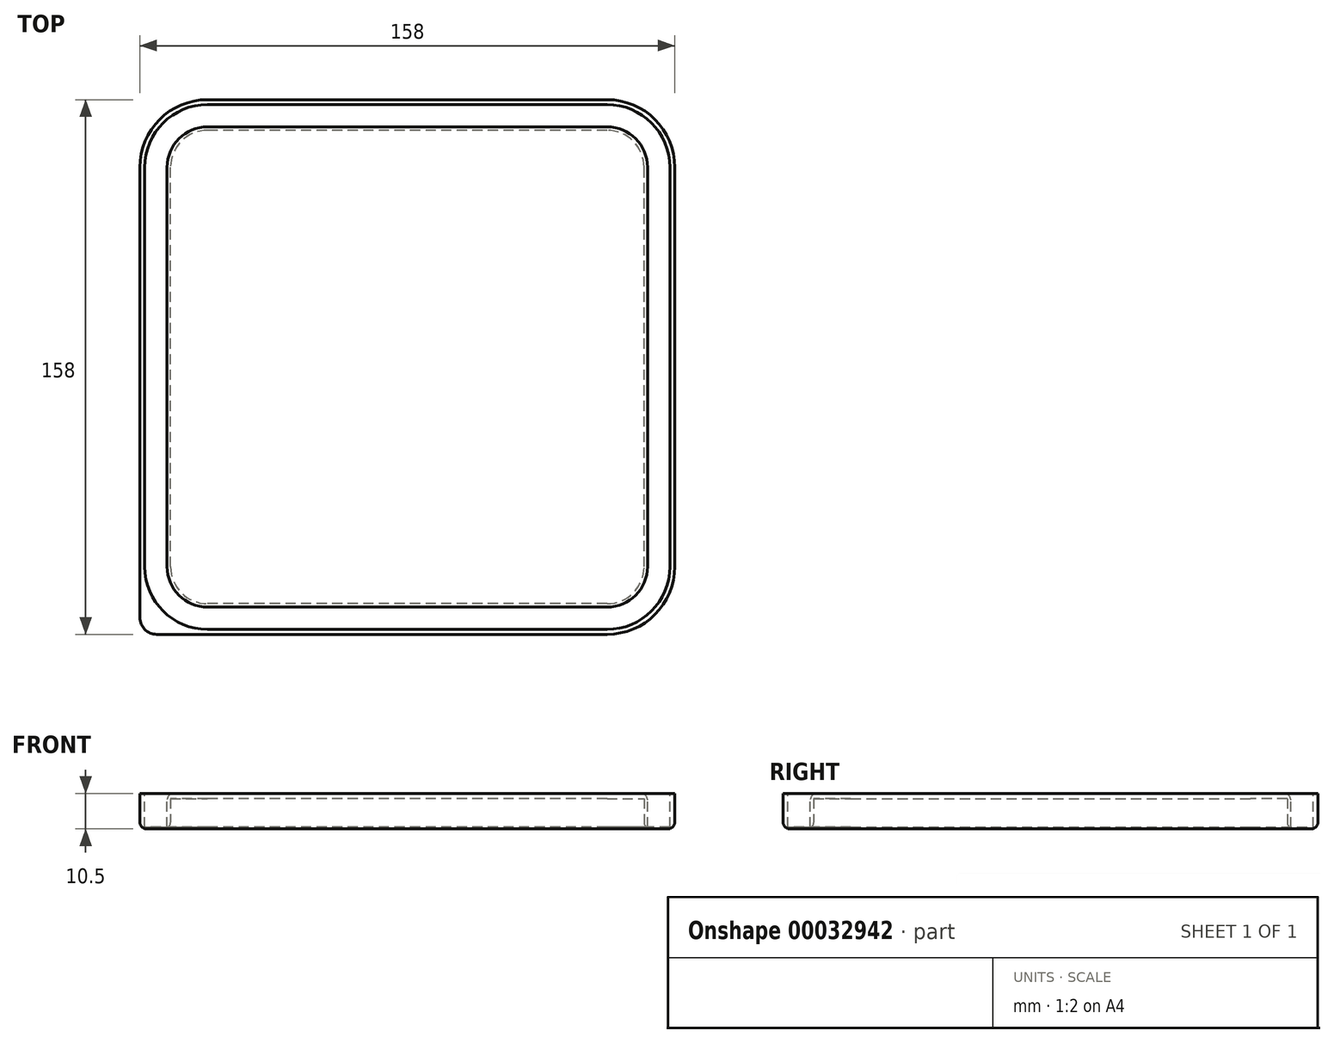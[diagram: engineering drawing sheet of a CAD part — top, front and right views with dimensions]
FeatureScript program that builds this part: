
annotation { "Feature Type Name" : "Feature", "Feature Type Description" : "" }
export const myFeature = defineFeature(function(context is Context, id is Id, definition is map)
    precondition{}
    {
        {
            var Q0;
            Q0=qCreatedBy(makeId("Top.planeOp"),FACE);
            var sketch = newSketch(context, id + "F0", { "sketchPlane" : qUnion([Q0])});
            skLineSegment(sketch, "E0.rect.bottom", {"start": v(59, -79) * mm, "end": v(-74, -79) * mm});
            skLineSegment(sketch, "E0.rect.top", {"start": v(59, 79) * mm, "end": v(-59, 79) * mm});
            skLineSegment(sketch, "E0.rect.left", {"start": v(79, -59) * mm, "end": v(79, 59) * mm});
            skLineSegment(sketch, "E0.rect.right", {"start": v(-79, -74) * mm, "end": v(-79, 59) * mm});
            skPoint(sketch, "E0.rect.middle", {"position": v(0, 0) * mm});
            skPoint(sketch, "E1.visualSharp", {"position": v(-79, 79) * mm});
            skArc(sketch, "E1.filletArc", {"start": v(-59, 79) * mm, "mid": v(-73.14, 73.14) * mm, "end": v(-79, 59) * mm});
            skPoint(sketch, "E2.visualSharp", {"position": v(79, 79) * mm});
            skArc(sketch, "E2.filletArc", {"start": v(79, 59) * mm, "mid": v(73.14, 73.14) * mm, "end": v(59, 79) * mm});
            skPoint(sketch, "E3.visualSharp", {"position": v(79, -79) * mm});
            skArc(sketch, "E3.filletArc", {"start": v(59, -79) * mm, "mid": v(73.14, -73.14) * mm, "end": v(79, -59) * mm});
            skPoint(sketch, "E4.visualSharp", {"position": v(-79, -79) * mm});
            skArc(sketch, "E4.filletArc", {"start": v(-79, -74) * mm, "mid": v(-77.54, -77.54) * mm, "end": v(-74, -79) * mm});
            skSolve(sketch);
        }
        {
            var Q0;
            Q0 = qSketchRegion(id + "F0", true);
            extrude(context, id + "F1", {"entities" : qUnion([Q0]), "depth" : 10.5 * mm});
        }
        {
            var Q0;
            Q0=makeQuery(id+"F1.opExtrude","CAP_FACE",FACE,{"disambiguationData":[OSD([sQuery(id+"F0.wireOp",EDGE,"E0.rect.bottom"),sQuery(id+"F0.wireOp",EDGE,"E0.rect.top"),sQuery(id+"F0.wireOp",EDGE,"E0.rect.left"),sQuery(id+"F0.wireOp",EDGE,"E0.rect.right"),sQuery(id+"F0.wireOp",EDGE,"E1.filletArc"),sQuery(id+"F0.wireOp",EDGE,"E2.filletArc"),sQuery(id+"F0.wireOp",EDGE,"E3.filletArc"),sQuery(id+"F0.wireOp",EDGE,"E4.filletArc")])],"isStart":false});
            var sketch = newSketch(context, id + "F2", { "sketchPlane" : qUnion([Q0])});
            skArc(sketch, "E5.0", {"start": v(77.55, 59) * mm, "mid": v(72.12, 72.12) * mm, "end": v(59, 77.55) * mm});
            skLineSegment(sketch, "E5.1", {"start": v(77.55, -59) * mm, "end": v(77.55, 59) * mm});
            skArc(sketch, "E5.2", {"start": v(59, -77.55) * mm, "mid": v(72.12, -72.12) * mm, "end": v(77.55, -59) * mm});
            skLineSegment(sketch, "E5.3", {"start": v(59, -77.55) * mm, "end": v(-59, -77.55) * mm});
            skArc(sketch, "E5.4", {"start": v(-77.55, -74) * mm, "mid": v(-76.51, -76.51) * mm, "end": v(-74, -77.55) * mm});
            skLineSegment(sketch, "E5.5", {"start": v(59, 77.55) * mm, "end": v(-59, 77.55) * mm});
            skLineSegment(sketch, "E5.6", {"start": v(-77.55, -59) * mm, "end": v(-77.55, 59) * mm});
            skArc(sketch, "E5.7", {"start": v(-59, 77.55) * mm, "mid": v(-72.12, 72.12) * mm, "end": v(-77.55, 59) * mm});
            skArc(sketch, "E6.0", {"start": v(70.95, 59) * mm, "mid": v(67.45, 67.45) * mm, "end": v(59, 70.95) * mm});
            skLineSegment(sketch, "E6.1", {"start": v(70.95, -59) * mm, "end": v(70.95, 59) * mm});
            skArc(sketch, "E6.2", {"start": v(59, -70.95) * mm, "mid": v(67.45, -67.45) * mm, "end": v(70.95, -59) * mm});
            skLineSegment(sketch, "E6.3", {"start": v(59, -70.95) * mm, "end": v(-59, -70.95) * mm});
            skLineSegment(sketch, "E6.4", {"start": v(-70.95, -59) * mm, "end": v(-70.95, 59) * mm});
            skLineSegment(sketch, "E6.5", {"start": v(59, 70.95) * mm, "end": v(-59, 70.95) * mm});
            skArc(sketch, "E6.6", {"start": v(-59, 70.95) * mm, "mid": v(-67.45, 67.45) * mm, "end": v(-70.95, 59) * mm});
            skPoint(sketch, "E7.visualSharp", {"position": v(-70.95, -70.95) * mm});
            skArc(sketch, "E7.filletArc", {"start": v(-70.95, -59) * mm, "mid": v(-67.45, -67.45) * mm, "end": v(-59, -70.95) * mm});
            skArc(sketch, "E8.filletArc", {"start": v(-77.55, -59) * mm, "mid": v(-72.12, -72.12) * mm, "end": v(-59, -77.55) * mm});
            skSolve(sketch);
        }
        {
            var Q0;
            Q0 = qSketchRegion(id + "F2", true);
            extrude(context, id + "F3", {"entities" : qUnion([Q0]), "operationType" : NewBodyOperationType.REMOVE, "oppositeDirection" : true, "depth" : 10 * mm});
        }
        {
            var Q0;
            Q0=makeQuery(id+"F1.opExtrude","CAP_FACE",FACE,{"disambiguationData":[OSD([sQuery(id+"F0.wireOp",EDGE,"E0.rect.bottom"),sQuery(id+"F0.wireOp",EDGE,"E0.rect.top"),sQuery(id+"F0.wireOp",EDGE,"E0.rect.left"),sQuery(id+"F0.wireOp",EDGE,"E0.rect.right"),sQuery(id+"F0.wireOp",EDGE,"E1.filletArc"),sQuery(id+"F0.wireOp",EDGE,"E2.filletArc"),sQuery(id+"F0.wireOp",EDGE,"E3.filletArc"),sQuery(id+"F0.wireOp",EDGE,"E4.filletArc")])],"isStart":true});
            var sketch = newSketch(context, id + "F4", { "sketchPlane" : qUnion([Q0])});
            skArc(sketch, "E9.0", {"start": v(69.95, -59) * mm, "mid": v(66.74, -66.74) * mm, "end": v(59, -69.95) * mm});
            skLineSegment(sketch, "E9.1", {"start": v(69.95, 59) * mm, "end": v(69.95, -59) * mm});
            skArc(sketch, "E9.2", {"start": v(59, 69.95) * mm, "mid": v(66.74, 66.74) * mm, "end": v(69.95, 59) * mm});
            skLineSegment(sketch, "E9.3", {"start": v(59, 69.95) * mm, "end": v(-59, 69.95) * mm});
            skArc(sketch, "E9.4", {"start": v(-69.95, 59) * mm, "mid": v(-66.74, 66.74) * mm, "end": v(-59, 69.95) * mm});
            skLineSegment(sketch, "E9.5", {"start": v(59, -69.95) * mm, "end": v(-59, -69.95) * mm});
            skLineSegment(sketch, "E9.6", {"start": v(-69.95, 59) * mm, "end": v(-69.95, -59) * mm});
            skArc(sketch, "E9.7", {"start": v(-59, -69.95) * mm, "mid": v(-66.74, -66.74) * mm, "end": v(-69.95, -59) * mm});
            skSolve(sketch);
        }
        {
            var Q0;
            Q0 = qSketchRegion(id + "F4", true);
            extrude(context, id + "F5", {"entities" : qUnion([Q0]), "operationType" : NewBodyOperationType.REMOVE, "oppositeDirection" : true, "depth" : 9 * mm});
        }
        {
            var Q0;
            Q0=makeQuery(id+"F1.opExtrude","CAP_FACE",FACE,{"disambiguationData":[OSD([sQuery(id+"F0.wireOp",EDGE,"E0.rect.bottom"),sQuery(id+"F0.wireOp",EDGE,"E0.rect.top"),sQuery(id+"F0.wireOp",EDGE,"E0.rect.left"),sQuery(id+"F0.wireOp",EDGE,"E0.rect.right"),sQuery(id+"F0.wireOp",EDGE,"E1.filletArc"),sQuery(id+"F0.wireOp",EDGE,"E2.filletArc"),sQuery(id+"F0.wireOp",EDGE,"E3.filletArc"),sQuery(id+"F0.wireOp",EDGE,"E4.filletArc")])],"isStart":true});
            var Q1;
            Q1=makeQuery(id+"F3.boolean.opBoolean","SPLIT",FACE,{"disambiguationData":[TD([makeQuery(id+"F3.opExtrude","SWEPT_FACE",FACE,{"disambiguationData":[OSD([sQuery(id+"F2.wireOp",EDGE,"E6.0")])]})])],"derivedFrom":makeQuery(id+"F1.opExtrude","CAP_FACE",FACE,{"disambiguationData":[OSD([sQuery(id+"F0.wireOp",EDGE,"E0.rect.bottom"),sQuery(id+"F0.wireOp",EDGE,"E0.rect.top"),sQuery(id+"F0.wireOp",EDGE,"E0.rect.left"),sQuery(id+"F0.wireOp",EDGE,"E0.rect.right"),sQuery(id+"F0.wireOp",EDGE,"E1.filletArc"),sQuery(id+"F0.wireOp",EDGE,"E2.filletArc"),sQuery(id+"F0.wireOp",EDGE,"E3.filletArc"),sQuery(id+"F0.wireOp",EDGE,"E4.filletArc")])],"isStart":false})});
            fillet(context, id + "F6", {"entities" : qUnion([Q0, Q1]), "radius" : 2 * mm, "tangentPropagation" : true, "allowEdgeOverflow" : false});
        }
    });
